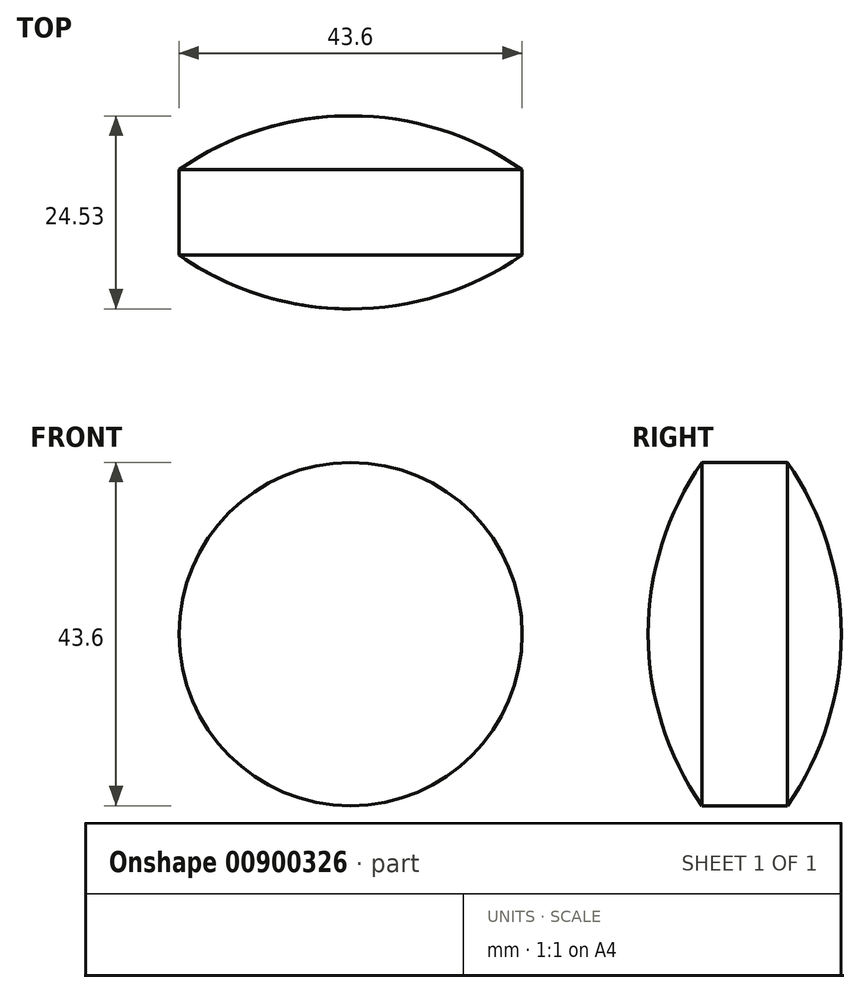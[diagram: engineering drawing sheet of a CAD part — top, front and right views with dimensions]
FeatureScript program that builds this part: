
annotation { "Feature Type Name" : "Feature", "Feature Type Description" : "" }
export const myFeature = defineFeature(function(context is Context, id is Id, definition is map)
    precondition{}
    {
        {
            var Q0;
            Q0=qCreatedBy(makeId("Top.planeOp"),FACE);
            var sketch = newSketch(context, id + "F0", { "sketchPlane" : qUnion([Q0])});
            skCircle(sketch, "E0", {"center": v(0, 0) * mm, "radius": 38.1 * mm});
            skLineSegment(sketch, "E1", {"start": v(0, 0) * mm, "end": v(0, -38.1) * mm});
            skCircle(sketch, "E2", {"center": v(0, 51.67) * mm, "radius": 38.1 * mm});
            skLineSegment(sketch, "E3.bottom", {"start": v(-21.8, 0) * mm, "end": v(21.8, 0) * mm});
            skLineSegment(sketch, "E3.top", {"start": v(-21.8, 67.83) * mm, "end": v(21.8, 67.83) * mm});
            skLineSegment(sketch, "E3.left", {"start": v(-21.8, 0) * mm, "end": v(-21.8, 67.83) * mm});
            skLineSegment(sketch, "E3.right", {"start": v(21.8, 0) * mm, "end": v(21.8, 67.83) * mm});
            skLineSegment(sketch, "E4", {"start": v(0, -38.1) * mm, "end": v(0, 89.77) * mm});
            skSolve(sketch);
        }
        {
            var Q0;
            {var subQ0=sQuery(id+"F0.wireOp",EDGE,"E3.left");var subQ1=sQuery(id+"F0.wireOp",EDGE,"E0");var subQ2=makeQuery(id+"F0.imprint","INTERSECT",VERTEX,{"derivedFrom":[subQ1,subQ0]});Q0=makeQuery(id+"F0.imprint","IMPRINT",FACE,{"disambiguationData":[TD([[makeQuery(id+"F0.imprint","IMPRINT",EDGE,{"disambiguationData":[TD([[subQ2,1.0]])],"derivedFrom":subQ1}),1.0]])]});}
            var Q1;
            Q1=sQuery(id+"F0.wireOp",EDGE,"E4");
            revolve(context, id + "F1", {"surfaceOperationType" : NewSurfaceOperationType.NEW, "entities" : qUnion([Q0]), "axis" : qUnion([Q1]), "revolveType" : RevolveType.FULL});
        }
    });
